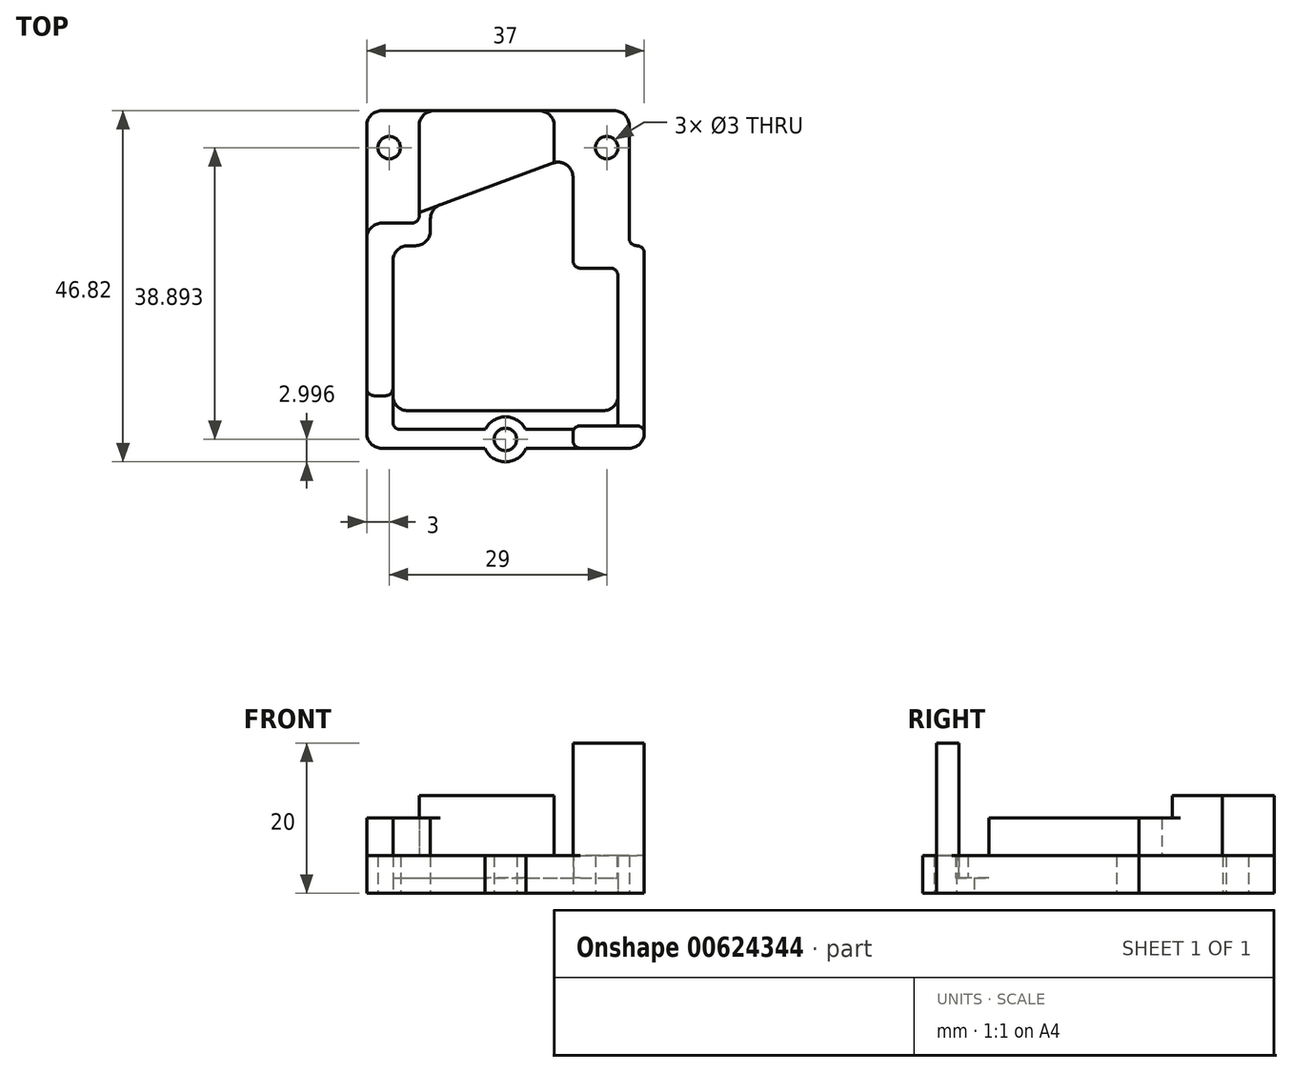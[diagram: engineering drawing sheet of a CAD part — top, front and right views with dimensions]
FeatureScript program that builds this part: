
annotation { "Feature Type Name" : "Feature", "Feature Type Description" : "" }
export const myFeature = defineFeature(function(context is Context, id is Id, definition is map)
    precondition{}
    {
        {
            var Q0;
            Q0=qCreatedBy(makeId("Top.planeOp"),FACE);
            var sketch = newSketch(context, id + "F0", { "sketchPlane" : qUnion([Q0])});
            skLineSegment(sketch, "E0.bottom", {"start": v(16.5, -22.5) * mm, "end": v(-16.5, -22.5) * mm});
            skLineSegment(sketch, "E0.top", {"start": v(14.5, 22.5) * mm, "end": v(-16.5, 22.5) * mm});
            skLineSegment(sketch, "E0.left", {"start": v(18.5, -20.5) * mm, "end": v(18.5, 3.5) * mm});
            skLineSegment(sketch, "E0.right", {"start": v(-18.5, -20.5) * mm, "end": v(-18.5, 20.5) * mm});
            skPoint(sketch, "E0.middle", {"position": v(0, 0) * mm});
            skLineSegment(sketch, "E1", {"start": v(-15, 2.5) * mm, "end": v(-15, -15.5) * mm});
            skLineSegment(sketch, "E2", {"start": v(-13, -17.5) * mm, "end": v(13, -17.5) * mm});
            skLineSegment(sketch, "E3", {"start": v(15, -15.5) * mm, "end": v(15, 0.5) * mm});
            skLineSegment(sketch, "E4", {"start": v(-13, 4.5) * mm, "end": v(-12, 4.5) * mm});
            skLineSegment(sketch, "E5", {"start": v(-10, 6.5) * mm, "end": v(-10, 8.1) * mm});
            skLineSegment(sketch, "E6", {"start": v(-8.7, 9.98) * mm, "end": v(6.3, 15.5) * mm});
            skLineSegment(sketch, "E7", {"start": v(9, 13.63) * mm, "end": v(9, 2.5) * mm});
            skLineSegment(sketch, "E8", {"start": v(10, 1.5) * mm, "end": v(14, 1.5) * mm});
            skLineSegment(sketch, "E9", {"start": v(16.5, 20.5) * mm, "end": v(16.5, 5.5) * mm});
            skLineSegment(sketch, "E10", {"start": v(17.5, 4.5) * mm, "end": v(17.5, 4.5) * mm});
            skPoint(sketch, "E11.visualSharp", {"position": v(-15, -17.5) * mm});
            skArc(sketch, "E11.filletArc", {"start": v(-15, -15.5) * mm, "mid": v(-14.41, -16.91) * mm, "end": v(-13, -17.5) * mm});
            skPoint(sketch, "E12.visualSharp", {"position": v(15, -17.5) * mm});
            skArc(sketch, "E12.filletArc", {"start": v(13, -17.5) * mm, "mid": v(14.41, -16.91) * mm, "end": v(15, -15.5) * mm});
            skPoint(sketch, "E13.visualSharp", {"position": v(-15, 4.5) * mm});
            skArc(sketch, "E13.filletArc", {"start": v(-13, 4.5) * mm, "mid": v(-14.41, 3.91) * mm, "end": v(-15, 2.5) * mm});
            skPoint(sketch, "E14.visualSharp", {"position": v(-10, 4.5) * mm});
            skArc(sketch, "E14.filletArc", {"start": v(-12, 4.5) * mm, "mid": v(-10.59, 5.09) * mm, "end": v(-10, 6.5) * mm});
            skPoint(sketch, "E15.visualSharp", {"position": v(-10, 9.5) * mm});
            skArc(sketch, "E15.filletArc", {"start": v(-8.7, 9.98) * mm, "mid": v(-9.64, 9.25) * mm, "end": v(-10, 8.1) * mm});
            skPoint(sketch, "E16.visualSharp", {"position": v(9, 16.5) * mm});
            skArc(sketch, "E16.filletArc", {"start": v(9, 13.63) * mm, "mid": v(8.14, 15.27) * mm, "end": v(6.3, 15.5) * mm});
            skPoint(sketch, "E17.visualSharp", {"position": v(-18.5, 22.5) * mm});
            skArc(sketch, "E17.filletArc", {"start": v(-16.5, 22.5) * mm, "mid": v(-17.91, 21.91) * mm, "end": v(-18.5, 20.5) * mm});
            skPoint(sketch, "E18.visualSharp", {"position": v(16.5, 22.5) * mm});
            skArc(sketch, "E18.filletArc", {"start": v(16.5, 20.5) * mm, "mid": v(15.91, 21.91) * mm, "end": v(14.5, 22.5) * mm});
            skPoint(sketch, "E19.visualSharp", {"position": v(18.5, -22.5) * mm});
            skArc(sketch, "E19.filletArc", {"start": v(16.5, -22.5) * mm, "mid": v(17.91, -21.91) * mm, "end": v(18.5, -20.5) * mm});
            skPoint(sketch, "E20.visualSharp", {"position": v(-18.5, -22.5) * mm});
            skArc(sketch, "E20.filletArc", {"start": v(-18.5, -20.5) * mm, "mid": v(-17.91, -21.91) * mm, "end": v(-16.5, -22.5) * mm});
            skPoint(sketch, "E21.visualSharp", {"position": v(9, 1.5) * mm});
            skArc(sketch, "E21.filletArc", {"start": v(9, 2.5) * mm, "mid": v(9.3, 1.8) * mm, "end": v(10, 1.5) * mm});
            skPoint(sketch, "E22.visualSharp", {"position": v(15, 1.5) * mm});
            skArc(sketch, "E22.filletArc", {"start": v(15, 0.5) * mm, "mid": v(14.7, 1.2) * mm, "end": v(14, 1.5) * mm});
            skPoint(sketch, "E23.visualSharp", {"position": v(16.5, 4.5) * mm});
            skArc(sketch, "E23.filletArc", {"start": v(16.5, 5.5) * mm, "mid": v(16.8, 4.8) * mm, "end": v(17.5, 4.5) * mm});
            skPoint(sketch, "E24.visualSharp", {"position": v(18.5, 4.5) * mm});
            skArc(sketch, "E24.filletArc", {"start": v(18.5, 3.5) * mm, "mid": v(18.2, 4.2) * mm, "end": v(17.5, 4.5) * mm});
            skLineSegment(sketch, "E25", {"start": v(-14, -20) * mm, "end": v(14, -20) * mm});
            skLineSegment(sketch, "E26", {"start": v(-15, -15.5) * mm, "end": v(-15, -19) * mm});
            skLineSegment(sketch, "E27", {"start": v(15, -15.5) * mm, "end": v(15, -19) * mm});
            skPoint(sketch, "E28.visualSharp", {"position": v(-15, -20) * mm});
            skArc(sketch, "E28.filletArc", {"start": v(-15, -19) * mm, "mid": v(-14.7, -19.7) * mm, "end": v(-14, -20) * mm});
            skPoint(sketch, "E29.visualSharp", {"position": v(15, -20) * mm});
            skArc(sketch, "E29.filletArc", {"start": v(14, -20) * mm, "mid": v(14.7, -19.7) * mm, "end": v(15, -19) * mm});
            skLineSegment(sketch, "E30", {"start": v(0, -17.5) * mm, "end": v(0, -27.49) * mm, "construction": true});
            skPoint(sketch, "E30.endSnap0", {"position": v(0, -22.5) * mm});
            skCircle(sketch, "E31", {"center": v(0, -21.32) * mm, "radius": 3 * mm});
            skCircle(sketch, "E32", {"center": v(0, -21.32) * mm, "radius": 1.5 * mm});
            skCircle(sketch, "E33", {"center": v(-15.5, 17.57) * mm, "radius": 3 * mm});
            skCircle(sketch, "E34", {"center": v(-15.5, 17.57) * mm, "radius": 1.5 * mm});
            skLineSegment(sketch, "E35", {"start": v(-15.5, 17.57) * mm, "end": v(14.82, 17.57) * mm, "construction": true});
            skCircle(sketch, "E36", {"center": v(13.5, 17.57) * mm, "radius": 3 * mm});
            skCircle(sketch, "E37", {"center": v(13.5, 17.57) * mm, "radius": 1.5 * mm});
            skSolve(sketch);
        }
        {
            var Q0;
            Q0=makeQuery(id+"F0.imprint","IMPRINT",FACE,{"disambiguationData":[TD([[makeQuery(id+"F0.imprint","IMPRINT",EDGE,{"derivedFrom":sQuery(id+"F0.wireOp",EDGE,"E2")}),-1.0]])]});
            extrude(context, id + "F1", {"entities" : qUnion([Q0]), "depth" : 2 * mm, "offsetDistance" : 25 * mm});
        }
        {
            var Q0;
            Q0=makeQuery(id+"F0.imprint","IMPRINT",FACE,{"disambiguationData":[TD([[makeQuery(id+"F0.imprint","IMPRINT",EDGE,{"derivedFrom":sQuery(id+"F0.wireOp",EDGE,"E0.top")}),1.0]])]});
            var Q1;
            {var subQ0=sQuery(id+"F0.wireOp",EDGE,"E31");var subQ1=sQuery(id+"F0.wireOp",EDGE,"E25");var subQ2=makeQuery(id+"F0.imprint","INTERSECT",VERTEX,{"disambiguationData":[OD(0.0)],"derivedFrom":[subQ1,subQ0]});Q1=makeQuery(id+"F0.imprint","IMPRINT",FACE,{"disambiguationData":[TD([[makeQuery(id+"F0.imprint","IMPRINT",EDGE,{"disambiguationData":[TD([[subQ2,-1.0]])],"derivedFrom":subQ1}),1.0]])]});}
            var Q2;
            {var subQ0=sQuery(id+"F0.wireOp",EDGE,"E31");var subQ1=sQuery(id+"F0.wireOp",EDGE,"E0.bottom");var subQ2=makeQuery(id+"F0.imprint","INTERSECT",VERTEX,{"disambiguationData":[OD(1.0)],"derivedFrom":[subQ1,subQ0]});Q2=makeQuery(id+"F0.imprint","IMPRINT",FACE,{"disambiguationData":[TD([[makeQuery(id+"F0.imprint","IMPRINT",EDGE,{"disambiguationData":[TD([[subQ2,1.0]])],"derivedFrom":subQ1}),-1.0]])]});}
            var Q3;
            {var subQ0=sQuery(id+"F0.wireOp",EDGE,"E31");var subQ1=sQuery(id+"F0.wireOp",EDGE,"E0.bottom");var subQ2=makeQuery(id+"F0.imprint","INTERSECT",VERTEX,{"disambiguationData":[OD(0.0)],"derivedFrom":[subQ1,subQ0]});Q3=makeQuery(id+"F0.imprint","IMPRINT",FACE,{"disambiguationData":[TD([[makeQuery(id+"F0.imprint","IMPRINT",EDGE,{"disambiguationData":[TD([[subQ2,-1.0]])],"derivedFrom":subQ1}),-1.0]])]});}
            var Q4;
            {var subQ0=sQuery(id+"F0.wireOp",EDGE,"E31");var subQ1=sQuery(id+"F0.wireOp",EDGE,"E0.bottom");var subQ2=makeQuery(id+"F0.imprint","INTERSECT",VERTEX,{"disambiguationData":[OD(0.0)],"derivedFrom":[subQ1,subQ0]});Q4=makeQuery(id+"F0.imprint","IMPRINT",FACE,{"disambiguationData":[TD([[makeQuery(id+"F0.imprint","IMPRINT",EDGE,{"disambiguationData":[TD([[subQ2,-1.0]])],"derivedFrom":subQ1}),1.0]])]});}
            var Q5;
            Q5=makeQuery(id+"F0.imprint","IMPRINT",FACE,{"disambiguationData":[TD([[makeQuery(id+"F0.imprint","IMPRINT",EDGE,{"derivedFrom":sQuery(id+"F0.wireOp",EDGE,"E33")}),1.0]])]});
            var Q6;
            Q6=makeQuery(id+"F0.imprint","IMPRINT",FACE,{"disambiguationData":[TD([[makeQuery(id+"F0.imprint","IMPRINT",EDGE,{"derivedFrom":sQuery(id+"F0.wireOp",EDGE,"E36")}),1.0]])]});
            extrude(context, id + "F2", {"entities" : qUnion([Q0, Q1, Q2, Q3, Q4, Q5, Q6]), "operationType" : NewBodyOperationType.ADD, "depth" : 5 * mm, "offsetDistance" : 25 * mm});
        }
        {
            var Q0;
            Q0=makeQuery(id+"F2.opExtrude","CAP_FACE",FACE,{"disambiguationData":[OSD([sQuery(id+"F0.wireOp",EDGE,"E0.bottom"),sQuery(id+"F0.wireOp",EDGE,"E0.top"),sQuery(id+"F0.wireOp",EDGE,"E0.left"),sQuery(id+"F0.wireOp",EDGE,"E0.right"),sQuery(id+"F0.wireOp",EDGE,"E1"),sQuery(id+"F0.wireOp",EDGE,"E3"),sQuery(id+"F0.wireOp",EDGE,"E4"),sQuery(id+"F0.wireOp",EDGE,"E5"),sQuery(id+"F0.wireOp",EDGE,"E6"),sQuery(id+"F0.wireOp",EDGE,"E7"),sQuery(id+"F0.wireOp",EDGE,"E8"),sQuery(id+"F0.wireOp",EDGE,"E9"),sQuery(id+"F0.wireOp",EDGE,"E13.filletArc"),sQuery(id+"F0.wireOp",EDGE,"E14.filletArc"),sQuery(id+"F0.wireOp",EDGE,"E15.filletArc"),sQuery(id+"F0.wireOp",EDGE,"E16.filletArc"),sQuery(id+"F0.wireOp",EDGE,"E17.filletArc"),sQuery(id+"F0.wireOp",EDGE,"E18.filletArc"),sQuery(id+"F0.wireOp",EDGE,"E19.filletArc"),sQuery(id+"F0.wireOp",EDGE,"E20.filletArc"),sQuery(id+"F0.wireOp",EDGE,"E21.filletArc"),sQuery(id+"F0.wireOp",EDGE,"E22.filletArc"),sQuery(id+"F0.wireOp",EDGE,"E23.filletArc"),sQuery(id+"F0.wireOp",EDGE,"E24.filletArc"),sQuery(id+"F0.wireOp",EDGE,"E25"),sQuery(id+"F0.wireOp",EDGE,"E26"),sQuery(id+"F0.wireOp",EDGE,"E27"),sQuery(id+"F0.wireOp",EDGE,"E28.filletArc"),sQuery(id+"F0.wireOp",EDGE,"E29.filletArc"),sQuery(id+"F0.wireOp",EDGE,"E31"),sQuery(id+"F0.wireOp",EDGE,"E32"),sQuery(id+"F0.wireOp",EDGE,"E34"),sQuery(id+"F0.wireOp",EDGE,"E37")])],"isStart":false});
            var sketch = newSketch(context, id + "F3", { "sketchPlane" : qUnion([Q0])});
            skLineSegment(sketch, "E38", {"start": v(-17.5, -15.5) * mm, "end": v(-16, -15.5) * mm});
            skLineSegment(sketch, "E39", {"start": v(-16.5, 7.5) * mm, "end": v(-12.5, 7.5) * mm});
            skLineSegment(sketch, "E40", {"start": v(-11.5, 8.5) * mm, "end": v(-11.5, 20.5) * mm});
            skLineSegment(sketch, "E41", {"start": v(6.5, 20.5) * mm, "end": v(6.5, 15.58) * mm});
            skLineSegment(sketch, "E42", {"start": v(-9.5, 22.5) * mm, "end": v(4.5, 22.5) * mm});
            skLineSegment(sketch, "E43", {"start": v(6.5, 15.58) * mm, "end": v(-11.5, 8.95) * mm});
            skLineSegment(sketch, "E44", {"start": v(-18.5, 5.5) * mm, "end": v(-18.5, -14.5) * mm});
            skLineSegment(sketch, "E45", {"start": v(-15, -14.5) * mm, "end": v(-15, 2.5) * mm});
            skPoint(sketch, "E46.visualSharp", {"position": v(-11.5, 22.5) * mm});
            skArc(sketch, "E46.filletArc", {"start": v(-9.5, 22.5) * mm, "mid": v(-10.91, 21.91) * mm, "end": v(-11.5, 20.5) * mm});
            skPoint(sketch, "E47.visualSharp", {"position": v(6.5, 22.5) * mm});
            skArc(sketch, "E47.filletArc", {"start": v(6.5, 20.5) * mm, "mid": v(5.91, 21.91) * mm, "end": v(4.5, 22.5) * mm});
            skPoint(sketch, "E48.visualSharp", {"position": v(-18.5, 7.5) * mm});
            skArc(sketch, "E48.filletArc", {"start": v(-16.5, 7.5) * mm, "mid": v(-17.91, 6.91) * mm, "end": v(-18.5, 5.5) * mm});
            skPoint(sketch, "E49.visualSharp", {"position": v(-18.5, -15.5) * mm});
            skArc(sketch, "E49.filletArc", {"start": v(-18.5, -14.5) * mm, "mid": v(-18.2, -15.2) * mm, "end": v(-17.5, -15.5) * mm});
            skPoint(sketch, "E50.visualSharp", {"position": v(-15, -15.5) * mm});
            skArc(sketch, "E50.filletArc", {"start": v(-16, -15.5) * mm, "mid": v(-15.3, -15.2) * mm, "end": v(-15, -14.5) * mm});
            skPoint(sketch, "E51.visualSharp", {"position": v(-11.5, 7.5) * mm});
            skArc(sketch, "E51.filletArc", {"start": v(-12.5, 7.5) * mm, "mid": v(-11.8, 7.8) * mm, "end": v(-11.5, 8.5) * mm});
            skLineSegment(sketch, "E52.bottom", {"start": v(10, 10.5) * mm, "end": v(15.5, 10.5) * mm});
            skLineSegment(sketch, "E52.top", {"start": v(10, 12.5) * mm, "end": v(15.5, 12.5) * mm});
            skLineSegment(sketch, "E52.left", {"start": v(9, 11.5) * mm, "end": v(9, 11.5) * mm});
            skLineSegment(sketch, "E52.right", {"start": v(16.5, 11.5) * mm, "end": v(16.5, 11.5) * mm});
            skLineSegment(sketch, "E53.bottom", {"start": v(10, 1.5) * mm, "end": v(17.5, 1.5) * mm});
            skLineSegment(sketch, "E53.top", {"start": v(10, 4.5) * mm, "end": v(17.5, 4.5) * mm});
            skLineSegment(sketch, "E53.left", {"start": v(9, 2.5) * mm, "end": v(9, 3.5) * mm});
            skLineSegment(sketch, "E53.right", {"start": v(18.5, 2.5) * mm, "end": v(18.5, 3.5) * mm});
            skLineSegment(sketch, "E54.bottom", {"start": v(10, -22.5) * mm, "end": v(16.5, -22.5) * mm});
            skLineSegment(sketch, "E54.top", {"start": v(10, -19.5) * mm, "end": v(17.5, -19.5) * mm});
            skLineSegment(sketch, "E54.left", {"start": v(9, -21.5) * mm, "end": v(9, -20.5) * mm});
            skLineSegment(sketch, "E54.right", {"start": v(18.5, -20.5) * mm, "end": v(18.5, -20.5) * mm});
            skLineSegment(sketch, "E55.bottom", {"start": v(13.25, 1.5) * mm, "end": v(12.25, 1.5) * mm});
            skLineSegment(sketch, "E55.left", {"start": v(13.25, 4.5) * mm, "end": v(13.25, 10.5) * mm});
            skLineSegment(sketch, "E55.right", {"start": v(12.25, 4.5) * mm, "end": v(12.25, 10.5) * mm});
            skPoint(sketch, "E55.middle", {"position": v(12.75, 10.5) * mm});
            skPoint(sketch, "E56.visualSharp", {"position": v(9, 12.5) * mm});
            skArc(sketch, "E56.filletArc", {"start": v(10, 12.5) * mm, "mid": v(9.3, 12.2) * mm, "end": v(9, 11.5) * mm});
            skPoint(sketch, "E57.visualSharp", {"position": v(9, 10.5) * mm});
            skArc(sketch, "E57.filletArc", {"start": v(9, 11.5) * mm, "mid": v(9.3, 10.8) * mm, "end": v(10, 10.5) * mm});
            skPoint(sketch, "E58.visualSharp", {"position": v(16.5, 10.5) * mm});
            skArc(sketch, "E58.filletArc", {"start": v(15.5, 10.5) * mm, "mid": v(16.2, 10.8) * mm, "end": v(16.5, 11.5) * mm});
            skPoint(sketch, "E59.visualSharp", {"position": v(16.5, 12.5) * mm});
            skArc(sketch, "E59.filletArc", {"start": v(16.5, 11.5) * mm, "mid": v(16.2, 12.2) * mm, "end": v(15.5, 12.5) * mm});
            skPoint(sketch, "E60.visualSharp", {"position": v(9, 4.5) * mm});
            skArc(sketch, "E60.filletArc", {"start": v(10, 4.5) * mm, "mid": v(9.3, 4.2) * mm, "end": v(9, 3.5) * mm});
            skPoint(sketch, "E61.visualSharp", {"position": v(18.5, 1.5) * mm});
            skArc(sketch, "E61.filletArc", {"start": v(17.5, 1.5) * mm, "mid": v(18.2, 1.8) * mm, "end": v(18.5, 2.5) * mm});
            skPoint(sketch, "E62.visualSharp", {"position": v(9, 1.5) * mm});
            skArc(sketch, "E62.filletArc", {"start": v(9, 2.5) * mm, "mid": v(9.3, 1.8) * mm, "end": v(10, 1.5) * mm});
            skPoint(sketch, "E63.visualSharp", {"position": v(18.5, 4.5) * mm});
            skArc(sketch, "E63.filletArc", {"start": v(18.5, 3.5) * mm, "mid": v(18.2, 4.2) * mm, "end": v(17.5, 4.5) * mm});
            skPoint(sketch, "E64.visualSharp", {"position": v(18.5, -19.5) * mm});
            skArc(sketch, "E64.filletArc", {"start": v(18.5, -20.5) * mm, "mid": v(18.2, -19.8) * mm, "end": v(17.5, -19.5) * mm});
            skPoint(sketch, "E65.visualSharp", {"position": v(9, -19.5) * mm});
            skArc(sketch, "E65.filletArc", {"start": v(10, -19.5) * mm, "mid": v(9.3, -19.8) * mm, "end": v(9, -20.5) * mm});
            skPoint(sketch, "E66.visualSharp", {"position": v(9, -22.5) * mm});
            skArc(sketch, "E66.filletArc", {"start": v(9, -21.5) * mm, "mid": v(9.3, -22.2) * mm, "end": v(10, -22.5) * mm});
            skPoint(sketch, "E67.visualSharp", {"position": v(18.5, -22.5) * mm});
            skArc(sketch, "E67.filletArc", {"start": v(16.5, -22.5) * mm, "mid": v(17.91, -21.91) * mm, "end": v(18.5, -20.5) * mm});
            skSolve(sketch);
        }
        {
            var Q0;
            Q0=makeQuery(id+"F3.imprint","IMPRINT",FACE,{"disambiguationData":[TD([[makeQuery(id+"F3.imprint","IMPRINT",EDGE,{"derivedFrom":sQuery(id+"F3.wireOp",EDGE,"E38")}),1.0]])]});
            extrude(context, id + "F4", {"entities" : qUnion([Q0]), "operationType" : NewBodyOperationType.ADD, "depth" : 5 * mm, "offsetDistance" : 25 * mm});
        }
        {
            var Q0;
            {var subQ2=sQuery(id+"F3.wireOp",EDGE,"E41");Q0=makeQuery(id+"F3.imprint","IMPRINT",FACE,{"disambiguationData":[TD([[makeQuery(id+"F3.imprint","IMPRINT",EDGE,{"derivedFrom":subQ2}),-1.0]])]});}
            extrude(context, id + "F5", {"entities" : qUnion([Q0]), "operationType" : NewBodyOperationType.ADD, "depth" : 8 * mm, "offsetDistance" : 25 * mm});
        }
        {
            var Q0;
            {var subQ0=sQuery(id+"F3.wireOp",EDGE,"E65.filletArc");var subQ1=sQuery(id+"F3.wireOp",EDGE,"E54.top");var subQ2=makeQuery(id+"F3.imprint","INTERSECT",VERTEX,{"derivedFrom":[subQ1,subQ0]});Q0=makeQuery(id+"F3.imprint","IMPRINT",FACE,{"disambiguationData":[TD([[makeQuery(id+"F3.imprint","IMPRINT",EDGE,{"disambiguationData":[TD([[subQ2,-1.0]])],"derivedFrom":subQ1}),-1.0]])]});}
            var Q1;
            Q1=makeQuery(id+"F3.imprint","IMPRINT",FACE,{"disambiguationData":[TD([[makeQuery(id+"F3.imprint","IMPRINT",EDGE,{"derivedFrom":sQuery(id+"F3.wireOp",EDGE,"E54.bottom")}),-1.0]])]});
            extrude(context, id + "F6", {"entities" : qUnion([Q0, Q1]), "operationType" : NewBodyOperationType.ADD, "oppositeDirection" : true, "depth" : 4 * mm, "offsetDistance" : 25 * mm});
        }
        {
            var Q0;
            {var subQ0=sQuery(id+"F3.wireOp",EDGE,"E65.filletArc");var subQ1=sQuery(id+"F3.wireOp",EDGE,"E54.top");var subQ2=makeQuery(id+"F3.imprint","INTERSECT",VERTEX,{"derivedFrom":[subQ1,subQ0]});Q0=makeQuery(id+"F3.imprint","IMPRINT",FACE,{"disambiguationData":[TD([[makeQuery(id+"F3.imprint","IMPRINT",EDGE,{"disambiguationData":[TD([[subQ2,-1.0]])],"derivedFrom":subQ1}),-1.0]])]});}
            var Q1;
            Q1=makeQuery(id+"F3.imprint","IMPRINT",FACE,{"disambiguationData":[TD([[makeQuery(id+"F3.imprint","IMPRINT",EDGE,{"derivedFrom":sQuery(id+"F3.wireOp",EDGE,"E54.bottom")}),-1.0]])]});
            extrude(context, id + "F7", {"entities" : qUnion([Q0, Q1]), "operationType" : NewBodyOperationType.ADD, "depth" : 15 * mm, "offsetDistance" : 25 * mm});
        }
    });
